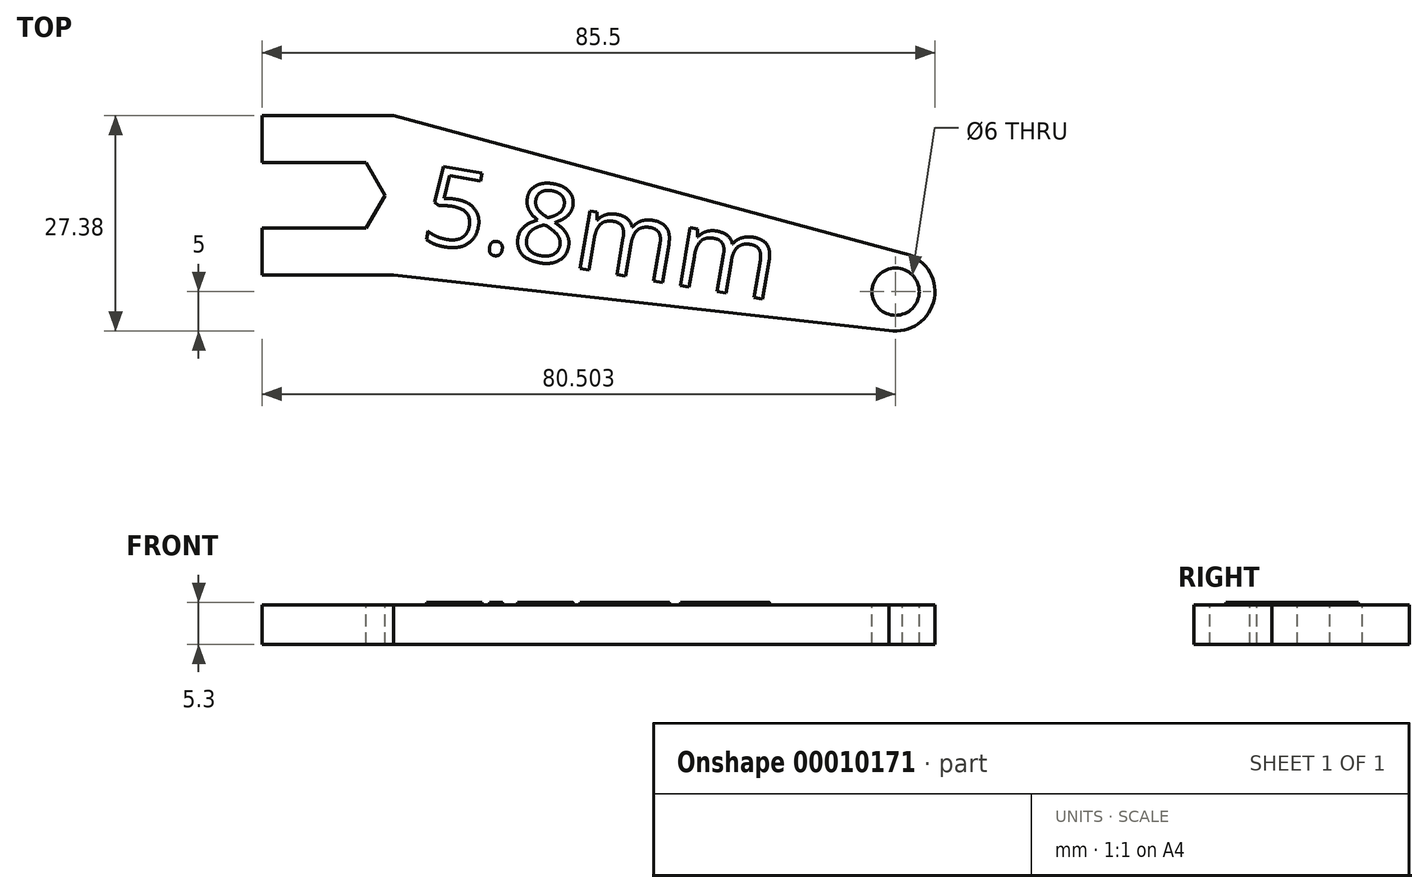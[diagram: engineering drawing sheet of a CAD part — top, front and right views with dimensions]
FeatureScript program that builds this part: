
annotation { "Feature Type Name" : "Feature", "Feature Type Description" : "" }
export const myFeature = defineFeature(function(context is Context, id is Id, definition is map)
    precondition{}
    {
        {
            var Q0;
            Q0=qCreatedBy(makeId("Top.planeOp"),FACE);
            var sketch = newSketch(context, id + "F0", { "sketchPlane" : qUnion([Q0])});
            skCircle(sketch, "E0.cCircle", {"center": v(-19.44, 8.62) * mm, "radius": 4.14 * mm, "construction": true});
            skLineSegment(sketch, "E0.0", {"start": v(-14.66, 8.62) * mm, "end": v(-17.05, 4.48) * mm});
            skLineSegment(sketch, "E0.1", {"start": v(-17.05, 4.48) * mm, "end": v(-21.83, 4.48) * mm});
            skLineSegment(sketch, "E0.2", {"start": v(-21.83, 4.48) * mm, "end": v(-24.22, 8.62) * mm, "construction": true});
            skLineSegment(sketch, "E0.3", {"start": v(-24.22, 8.62) * mm, "end": v(-21.83, 12.75) * mm, "construction": true});
            skLineSegment(sketch, "E0.4", {"start": v(-21.83, 12.75) * mm, "end": v(-17.05, 12.75) * mm});
            skLineSegment(sketch, "E0.5", {"start": v(-17.05, 12.75) * mm, "end": v(-14.66, 8.62) * mm});
            skPoint(sketch, "E0.0.midPoint", {"position": v(-15.86, 6.55) * mm});
            skCircle(sketch, "E1.cCircle", {"center": v(-19.44, 8.62) * mm, "radius": 10.14 * mm, "construction": true});
            skLineSegment(sketch, "E1.0", {"start": v(-13.59, 18.75) * mm, "end": v(-7.74, 8.62) * mm, "construction": true});
            skLineSegment(sketch, "E1.1", {"start": v(-7.74, 8.62) * mm, "end": v(-13.59, -1.52) * mm, "construction": true});
            skLineSegment(sketch, "E1.2", {"start": v(-13.59, -1.52) * mm, "end": v(-23.13, -1.52) * mm});
            skLineSegment(sketch, "E1.3", {"start": v(-23.13, -1.52) * mm, "end": v(-30.3, 4.48) * mm, "construction": true});
            skLineSegment(sketch, "E1.4", {"start": v(-30.3, 12.75) * mm, "end": v(-23.13, 18.75) * mm, "construction": true});
            skLineSegment(sketch, "E1.5", {"start": v(-23.13, 18.75) * mm, "end": v(-13.59, 18.75) * mm});
            skPoint(sketch, "E1.0.midPoint", {"position": v(-10.66, 13.69) * mm});
            skLineSegment(sketch, "E2", {"start": v(-30.3, 12.75) * mm, "end": v(-21.83, 12.75) * mm});
            skLineSegment(sketch, "E3", {"start": v(-30.3, 4.48) * mm, "end": v(-21.83, 4.48) * mm});
            skLineSegment(sketch, "E4", {"start": v(-23.13, 18.75) * mm, "end": v(-30.3, 18.75) * mm});
            skLineSegment(sketch, "E5", {"start": v(-30.3, 18.75) * mm, "end": v(-30.3, 12.75) * mm});
            skLineSegment(sketch, "E6", {"start": v(-30.3, 4.48) * mm, "end": v(-30.3, -1.52) * mm});
            skLineSegment(sketch, "E7", {"start": v(-30.3, -1.52) * mm, "end": v(-23.13, -1.52) * mm});
            skLineSegment(sketch, "E8", {"start": v(-19.44, 8.62) * mm, "end": v(-17.05, 12.75) * mm, "construction": true});
            skLineSegment(sketch, "E9.right", {"start": v(51.08, 1.3) * mm, "end": v(49.34, -8.55) * mm, "construction": true});
            skArc(sketch, "E10", {"start": v(49.34, -8.55) * mm, "mid": v(55.14, -4.5) * mm, "end": v(51.08, 1.3) * mm});
            skCircle(sketch, "E11", {"center": v(50.21, -3.63) * mm, "radius": 3 * mm});
            skLineSegment(sketch, "E12", {"start": v(-13.59, 18.75) * mm, "end": v(51.08, 1.3) * mm});
            skLineSegment(sketch, "E13", {"start": v(49.34, -8.55) * mm, "end": v(-13.59, -1.52) * mm});
            skSolve(sketch);
        }
        {
            var Q0;
            Q0=makeQuery(id+"F0.imprint","IMPRINT",FACE,{"disambiguationData":[TD([[makeQuery(id+"F0.imprint","IMPRINT",EDGE,{"derivedFrom":sQuery(id+"F0.wireOp",EDGE,"E0.0")}),1.0]])]});
            extrude(context, id + "F1", {"entities" : qUnion([Q0]), "oppositeDirection" : true, "depth" : 5 * mm});
        }
        {
            var Q0;
            Q0=qCreatedBy(makeId("Top.planeOp"),FACE);
            var sketch = newSketch(context, id + "F2", { "sketchPlane" : qUnion([Q0])});
            skText(sketch, "E14", { "text": "5.8mm", "fontName": "OpenSans-Regular.ttf"});
            const initialGuessF2  = {"E14": [-0.01034, 0.00276, 0.98615, -0.16585, 0.01]};
            skSetInitialGuess(sketch, initialGuessF2);
            skSolve(sketch);
        }
        {
            var Q0;
            Q0=makeQuery(id+"F2.imprint","IMPRINT",FACE,{"disambiguationData":[TD([[makeQuery(id+"F2.imprint","IMPRINT",EDGE,{"derivedFrom":sQuery(id+"F2.wireOp",EDGE,"E14.sketch_text.stroke-0")}),-1.0]])]});
            var Q1;
            Q1=makeQuery(id+"F2.imprint","IMPRINT",FACE,{"disambiguationData":[TD([[makeQuery(id+"F2.imprint","IMPRINT",EDGE,{"derivedFrom":sQuery(id+"F2.wireOp",EDGE,"E14.sketch_text.stroke-19")}),-1.0]])]});
            var Q2;
            Q2=makeQuery(id+"F2.imprint","IMPRINT",FACE,{"disambiguationData":[TD([[makeQuery(id+"F2.imprint","IMPRINT",EDGE,{"derivedFrom":sQuery(id+"F2.wireOp",EDGE,"E14.sketch_text.stroke-58")}),-1.0]])]});
            var Q3;
            Q3=makeQuery(id+"F2.imprint","IMPRINT",FACE,{"disambiguationData":[TD([[makeQuery(id+"F2.imprint","IMPRINT",EDGE,{"derivedFrom":sQuery(id+"F2.wireOp",EDGE,"E14.sketch_text.stroke-86")}),-1.0]])]});
            var Q4;
            Q4=makeQuery(id+"F2.imprint","IMPRINT",FACE,{"disambiguationData":[TD([[makeQuery(id+"F2.imprint","IMPRINT",EDGE,{"derivedFrom":sQuery(id+"F2.wireOp",EDGE,"E14.sketch_text.stroke-27")}),-1.0]])]});
            extrude(context, id + "F3", {"entities" : qUnion([Q0, Q1, Q2, Q3, Q4]), "operationType" : NewBodyOperationType.ADD, "depth" : 0.3 * mm});
        }
    });
